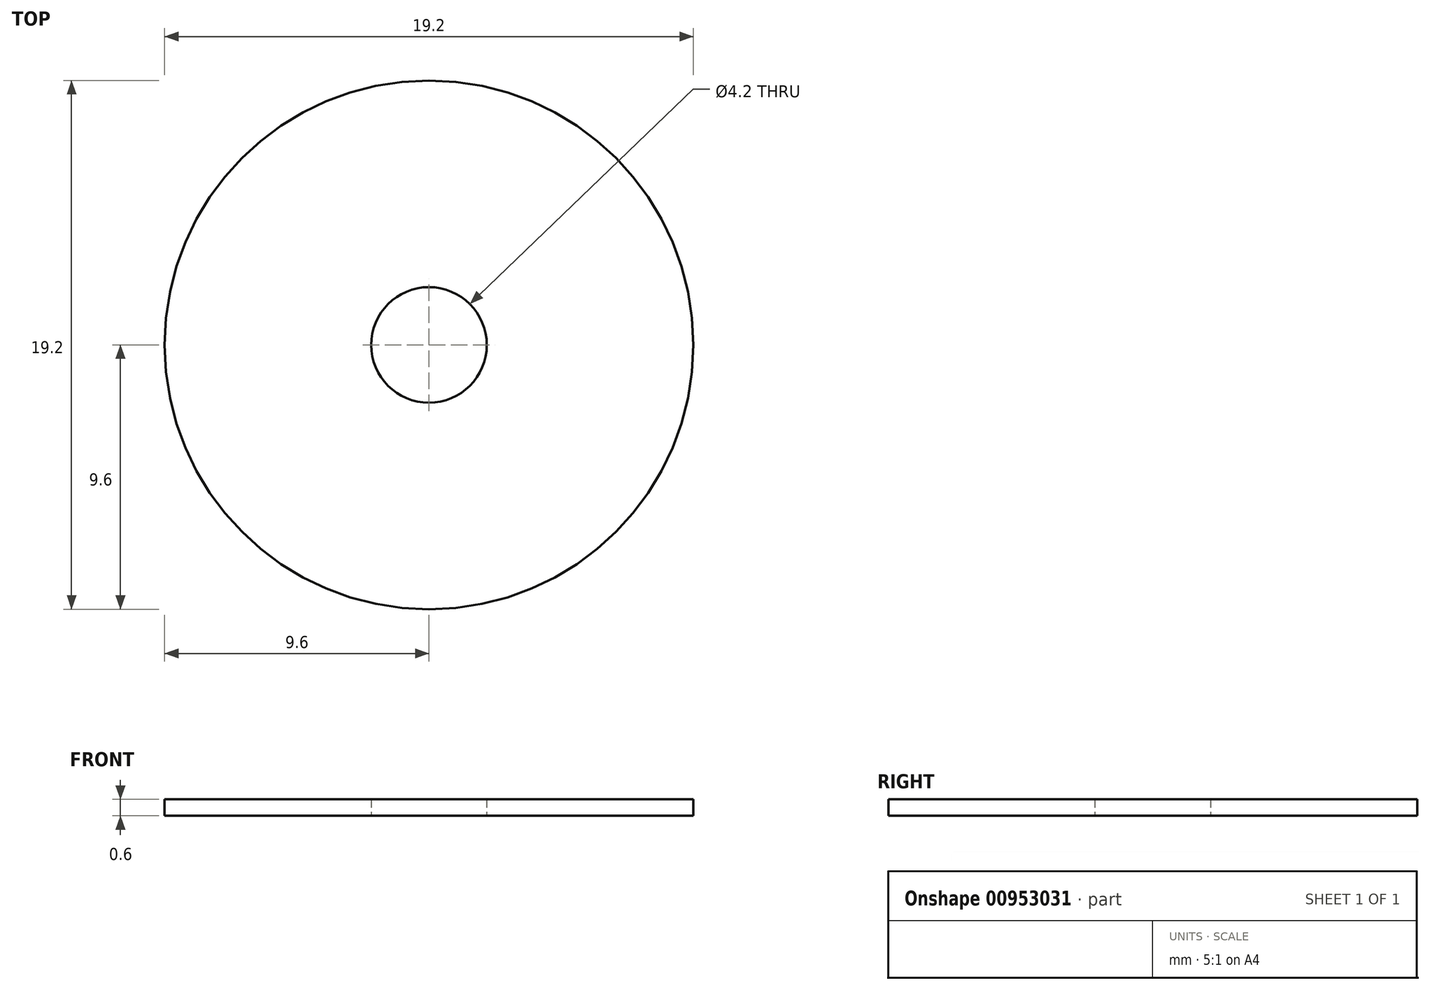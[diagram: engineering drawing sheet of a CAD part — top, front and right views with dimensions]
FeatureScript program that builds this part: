
annotation { "Feature Type Name" : "Feature", "Feature Type Description" : "" }
export const myFeature = defineFeature(function(context is Context, id is Id, definition is map)
    precondition{}
    {
        {
            var Q0;
            Q0=qCreatedBy(makeId("Top.planeOp"),FACE);
            var sketch = newSketch(context, id + "F0", { "sketchPlane" : qUnion([Q0])});
            skCircle(sketch, "E0", {"center": v(0, 0) * mm, "radius": 2.1 * mm});
            skCircle(sketch, "E1", {"center": v(0, 0) * mm, "radius": 9.6 * mm});
            skSolve(sketch);
        }
        {
            var Q0;
            Q0=makeQuery(id+"F0.imprint","IMPRINT",FACE,{"disambiguationData":[TD([[makeQuery(id+"F0.imprint","IMPRINT",EDGE,{"derivedFrom":sQuery(id+"F0.wireOp",EDGE,"E0")}),-1.0]])]});
            extrude(context, id + "F1", {"entities" : qUnion([Q0]), "depth" : 0.6 * mm, "offsetDistance" : 25 * mm});
        }
    });
